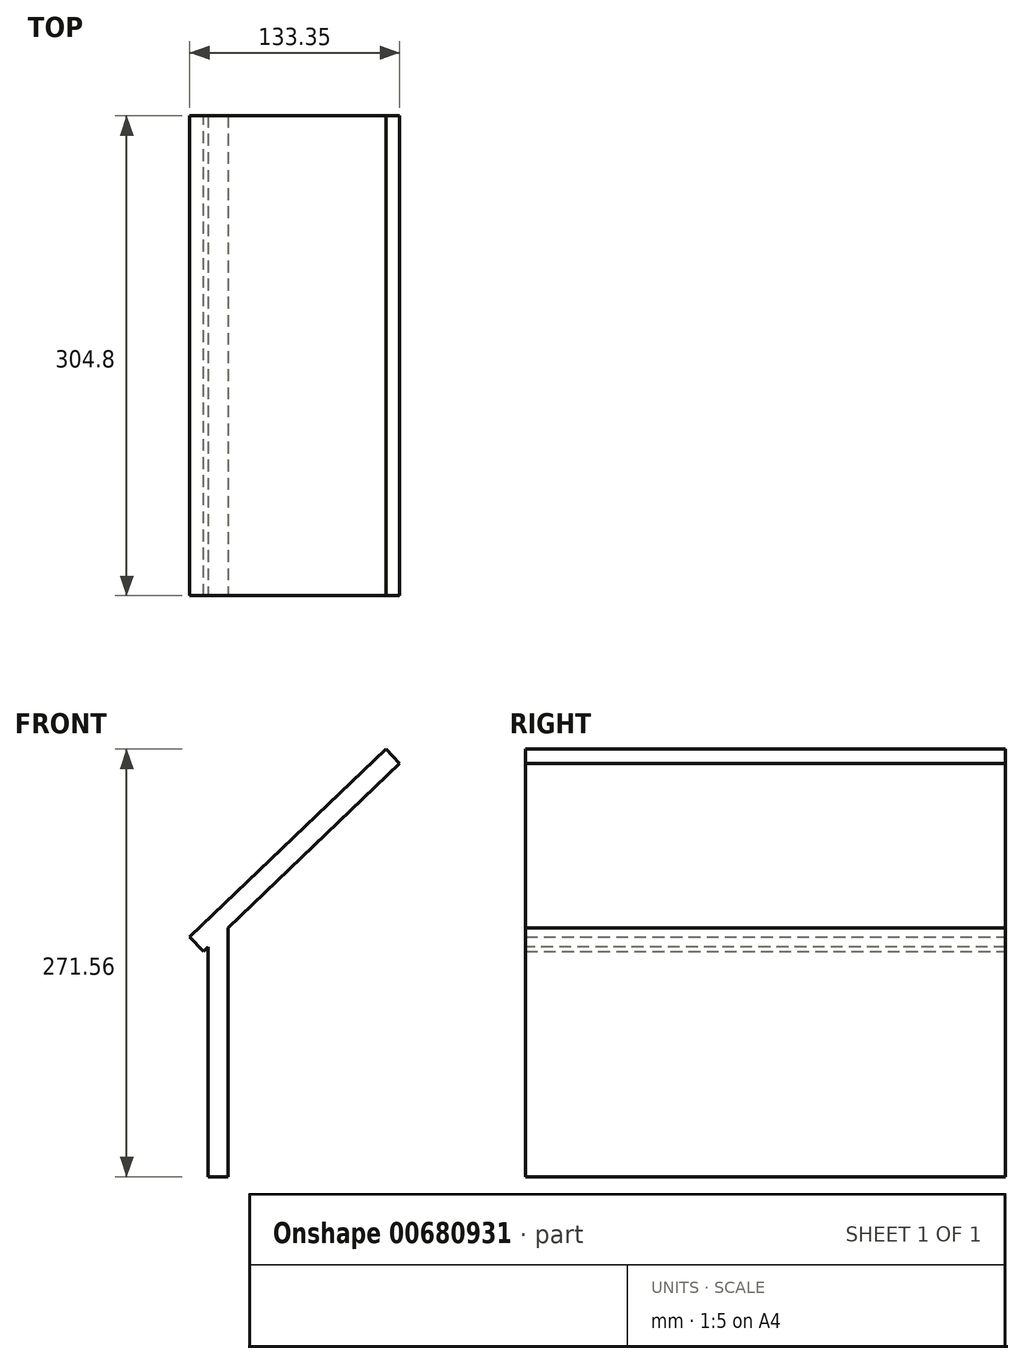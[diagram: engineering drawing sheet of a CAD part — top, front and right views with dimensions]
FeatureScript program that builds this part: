
annotation { "Feature Type Name" : "Feature", "Feature Type Description" : "" }
export const myFeature = defineFeature(function(context is Context, id is Id, definition is map)
    precondition{}
    {
        {
            var Q0;
            Q0=qCreatedBy(makeId("Front.planeOp"),FACE);
            var sketch = newSketch(context, id + "F0", { "sketchPlane" : qUnion([Q0])});
            skLineSegment(sketch, "E0.bottom", {"start": v(152.4, 152.4) * mm, "end": v(-152.4, 152.4) * mm});
            skLineSegment(sketch, "E0.top", {"start": v(152.4, -152.4) * mm, "end": v(-152.4, -152.4) * mm});
            skLineSegment(sketch, "E0.left", {"start": v(152.4, 152.4) * mm, "end": v(152.4, -152.4) * mm});
            skLineSegment(sketch, "E0.right", {"start": v(-152.4, 152.4) * mm, "end": v(-152.4, -152.4) * mm});
            skPoint(sketch, "E0.middle", {"position": v(0, 0) * mm});
            skLineSegment(sketch, "E1.bottom", {"start": v(-152.4, -152.4) * mm, "end": v(-139.7, -152.4) * mm});
            skLineSegment(sketch, "E1.top", {"start": v(-152.4, -114.3) * mm, "end": v(-139.7, -114.3) * mm});
            skLineSegment(sketch, "E1.left", {"start": v(-152.4, -152.4) * mm, "end": v(-152.4, -114.3) * mm});
            skLineSegment(sketch, "E1.right", {"start": v(-139.7, -152.4) * mm, "end": v(-139.7, -114.3) * mm});
            skLineSegment(sketch, "E2.bottom", {"start": v(-139.7, -152.4) * mm, "end": v(152.4, -152.4) * mm});
            skLineSegment(sketch, "E2.top", {"start": v(-139.7, -139.7) * mm, "end": v(152.4, -139.7) * mm});
            skLineSegment(sketch, "E2.left", {"start": v(-139.7, -152.4) * mm, "end": v(-139.7, -139.7) * mm});
            skLineSegment(sketch, "E2.right", {"start": v(152.4, -152.4) * mm, "end": v(152.4, -139.7) * mm});
            skLineSegment(sketch, "E3.bottom", {"start": v(152.4, -139.7) * mm, "end": v(139.7, -139.7) * mm});
            skLineSegment(sketch, "E3.top", {"start": v(152.4, 152.4) * mm, "end": v(139.7, 152.4) * mm});
            skLineSegment(sketch, "E3.left", {"start": v(152.4, -139.7) * mm, "end": v(152.4, 152.4) * mm});
            skLineSegment(sketch, "E3.right", {"start": v(139.7, -139.7) * mm, "end": v(139.7, 152.4) * mm});
            skLineSegment(sketch, "E4", {"start": v(-139.7, -139.7) * mm, "end": v(-139.7, -127) * mm});
            skLineSegment(sketch, "E5", {"start": v(-139.7, -127) * mm, "end": v(152.4, 152.4) * mm});
            skLineSegment(sketch, "E6", {"start": v(6.35, 12.7) * mm, "end": v(15.13, 3.52) * mm});
            skLineSegment(sketch, "E7", {"start": v(15.13, 3.52) * mm, "end": v(139.7, 122.68) * mm});
            skLineSegment(sketch, "E8", {"start": v(15.13, 3.52) * mm, "end": v(-134.6, -139.7) * mm});
            skLineSegment(sketch, "E9", {"start": v(139.7, 122.68) * mm, "end": v(152.4, 134.83) * mm});
            skSolve(sketch);
        }
        {
            var Q0;
            Q0=makeQuery(id+"F0.imprint","IMPRINT",FACE,{"disambiguationData":[TD([[makeQuery(id+"F0.imprint","IMPRINT",EDGE,{"derivedFrom":sQuery(id+"F0.wireOp",EDGE,"E1.bottom")}),1.0]])]});
            var Q1;
            {var subQ1=sQuery(id+"F0.wireOp",EDGE,"E4");Q1=makeQuery(id+"F0.imprint","IMPRINT",FACE,{"disambiguationData":[TD([[makeQuery(id+"F0.imprint","IMPRINT",EDGE,{"derivedFrom":subQ1}),-1.0]])]});}
            var Q2;
            Q2=makeQuery(id+"F0.imprint","IMPRINT",FACE,{"disambiguationData":[TD([[makeQuery(id+"F0.imprint","IMPRINT",EDGE,{"derivedFrom":sQuery(id+"F0.wireOp",EDGE,"E2.bottom")}),1.0]])]});
            var Q3;
            {var subQ4=sQuery(id+"F0.wireOp",EDGE,"E6");Q3=makeQuery(id+"F0.imprint","IMPRINT",FACE,{"disambiguationData":[TD([[makeQuery(id+"F0.imprint","IMPRINT",EDGE,{"derivedFrom":subQ4}),1.0]])]});}
            var Q4;
            {var subQ3=sQuery(id+"F0.wireOp",EDGE,"E9");Q4=makeQuery(id+"F0.imprint","IMPRINT",FACE,{"disambiguationData":[TD([[makeQuery(id+"F0.imprint","IMPRINT",EDGE,{"derivedFrom":subQ3}),1.0]])]});}
            var Q5;
            {var subQ0=sQuery(id+"F0.wireOp",EDGE,"E3.bottom");Q5=makeQuery(id+"F0.imprint","IMPRINT",FACE,{"disambiguationData":[TD([[makeQuery(id+"F0.imprint","IMPRINT",EDGE,{"derivedFrom":subQ0}),-1.0]])]});}
            extrude(context, id + "F1", {"entities" : qUnion([Q0, Q1, Q2, Q3, Q4, Q5]), "depth" : 304.8 * mm, "offsetDistance" : 25.4 * mm});
        }
        {
            var Q0;
            Q0=makeQuery(id+"F1.opExtrude","CAP_FACE",FACE,{"disambiguationData":[OSD([sQuery(id+"F0.wireOp",EDGE,"E1.bottom"),sQuery(id+"F0.wireOp",EDGE,"E1.top"),sQuery(id+"F0.wireOp",EDGE,"E1.left"),sQuery(id+"F0.wireOp",EDGE,"E1.right"),sQuery(id+"F0.wireOp",EDGE,"E2.bottom"),sQuery(id+"F0.wireOp",EDGE,"E2.top"),sQuery(id+"F0.wireOp",EDGE,"E2.right"),sQuery(id+"F0.wireOp",EDGE,"E3.left"),sQuery(id+"F0.wireOp",EDGE,"E3.right"),sQuery(id+"F0.wireOp",EDGE,"E5"),sQuery(id+"F0.wireOp",EDGE,"E7"),sQuery(id+"F0.wireOp",EDGE,"E8")])],"isStart":false});
            var sketch = newSketch(context, id + "F2", { "sketchPlane" : qUnion([Q0])});
            skLineSegment(sketch, "E10", {"start": v(-134.6, -139.7) * mm, "end": v(17.8, -139.7) * mm});
            skLineSegment(sketch, "E11", {"start": v(17.8, -139.7) * mm, "end": v(17.8, -88.9) * mm});
            skLineSegment(sketch, "E12", {"start": v(17.8, -88.9) * mm, "end": v(-81.5, -88.9) * mm});
            skLineSegment(sketch, "E13", {"start": v(17.8, -88.9) * mm, "end": v(17.8, -76.2) * mm});
            skLineSegment(sketch, "E14", {"start": v(17.8, -76.2) * mm, "end": v(-68.22, -76.2) * mm});
            skLineSegment(sketch, "E15.bottom", {"start": v(17.8, -139.7) * mm, "end": v(30.5, -139.7) * mm});
            skLineSegment(sketch, "E15.top", {"start": v(17.8, 18.22) * mm, "end": v(30.5, 18.22) * mm});
            skLineSegment(sketch, "E15.left", {"start": v(17.8, -139.7) * mm, "end": v(17.8, 18.22) * mm});
            skLineSegment(sketch, "E15.right", {"start": v(30.5, -139.7) * mm, "end": v(30.5, 18.22) * mm});
            skSolve(sketch);
        }
        {
            var Q0;
            {var subQ0=sQuery(id+"F2.wireOp",EDGE,"E12");Q0=makeQuery(id+"F2.imprint","IMPRINT",FACE,{"disambiguationData":[TD([[makeQuery(id+"F2.imprint","IMPRINT",EDGE,{"derivedFrom":subQ0}),-1.0]])]});}
            var Q1;
            {var subQ5=sQuery(id+"F2.wireOp",EDGE,"E15.bottom");Q1=makeQuery(id+"F2.imprint","IMPRINT",FACE,{"disambiguationData":[TD([[makeQuery(id+"F2.imprint","IMPRINT",EDGE,{"derivedFrom":subQ5}),1.0]])]});}
            extrude(context, id + "F3", {"entities" : qUnion([Q0, Q1]), "operationType" : NewBodyOperationType.ADD, "oppositeDirection" : true, "depth" : 304.8 * mm, "offsetDistance" : 25.4 * mm});
        }
        {
            var Q0;
            {var subQ0=sQuery(id+"F0.wireOp",EDGE,"E8");var subQ1=sQuery(id+"F0.wireOp",EDGE,"E7");Q0=makeQuery(id+"F3.boolean.opBoolean","MERGE",FACE,{"derivedFrom":[makeQuery(id+"F1.opExtrude","CAP_FACE",FACE,{"disambiguationData":[OSD([sQuery(id+"F0.wireOp",EDGE,"E1.bottom"),sQuery(id+"F0.wireOp",EDGE,"E1.top"),sQuery(id+"F0.wireOp",EDGE,"E1.left"),sQuery(id+"F0.wireOp",EDGE,"E1.right"),sQuery(id+"F0.wireOp",EDGE,"E2.bottom"),sQuery(id+"F0.wireOp",EDGE,"E2.top"),sQuery(id+"F0.wireOp",EDGE,"E2.right"),sQuery(id+"F0.wireOp",EDGE,"E3.left"),sQuery(id+"F0.wireOp",EDGE,"E3.right"),sQuery(id+"F0.wireOp",EDGE,"E5"),subQ1,subQ0])],"isStart":false}),makeQuery(id+"F3.opExtrude","CAP_FACE",FACE,{"disambiguationData":[OSD([subQ1,subQ0,sQuery(id+"F2.wireOp",EDGE,"E12"),sQuery(id+"F2.wireOp",EDGE,"E14"),sQuery(id+"F2.wireOp",EDGE,"E15.bottom"),sQuery(id+"F2.wireOp",EDGE,"E15.left"),sQuery(id+"F2.wireOp",EDGE,"E15.right")])],"isStart":true})]});}
            var sketch = newSketch(context, id + "F4", { "sketchPlane" : qUnion([Q0])});
            skLineSegment(sketch, "E16", {"start": v(139.7, 122.68) * mm, "end": v(130.92, 131.86) * mm});
            skLineSegment(sketch, "E17", {"start": v(139.7, -139.7) * mm, "end": v(139.7, -152.4) * mm});
            skSolve(sketch);
        }
        {
            var Q0;
            {var subQ2=sQuery(id+"F4.wireOp",EDGE,"E16");Q0=makeQuery(id+"F4.imprint","IMPRINT",FACE,{"disambiguationData":[TD([[makeQuery(id+"F4.imprint","IMPRINT",EDGE,{"derivedFrom":subQ2}),-1.0]])]});}
            extrude(context, id + "F5", {"entities" : qUnion([Q0]), "operationType" : NewBodyOperationType.REMOVE, "oppositeDirection" : true, "depth" : 304.8 * mm, "offsetDistance" : 25.4 * mm});
        }
    });
